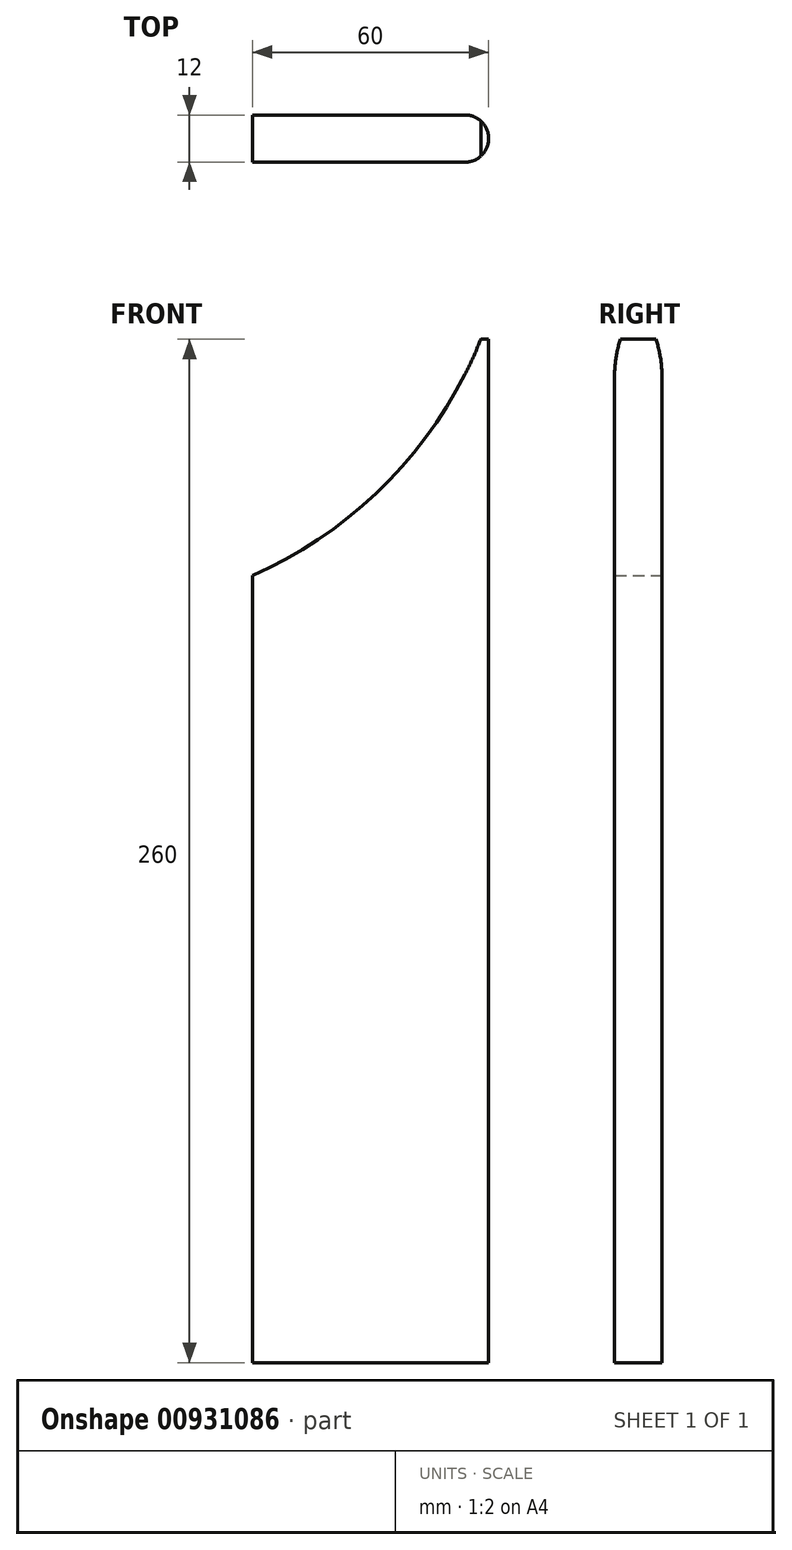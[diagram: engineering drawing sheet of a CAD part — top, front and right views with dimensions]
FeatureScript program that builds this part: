
annotation { "Feature Type Name" : "Feature", "Feature Type Description" : "" }
export const myFeature = defineFeature(function(context is Context, id is Id, definition is map)
    precondition{}
    {
        {
            var Q0;
            Q0=qCreatedBy(makeId("Front.planeOp"),FACE);
            var sketch = newSketch(context, id + "F0", { "sketchPlane" : qUnion([Q0])});
            skLineSegment(sketch, "E0.bottom", {"start": v(0, 0) * mm, "end": v(60, 0) * mm});
            skLineSegment(sketch, "E0.top", {"start": v(58, 260) * mm, "end": v(60, 260) * mm});
            skLineSegment(sketch, "E0.left", {"start": v(0, 0) * mm, "end": v(0, 200) * mm});
            skLineSegment(sketch, "E0.right", {"start": v(60, 0) * mm, "end": v(60, 260) * mm});
            skArc(sketch, "E1", {"start": v(0, 200) * mm, "mid": v(34.91, 224.29) * mm, "end": v(58, 260) * mm});
            skSolve(sketch);
        }
        {
            var Q0;
            Q0=makeQuery(id+"F0.imprint","IMPRINT",FACE,{"disambiguationData":[TD([[makeQuery(id+"F0.imprint","IMPRINT",EDGE,{"derivedFrom":sQuery(id+"F0.wireOp",EDGE,"E0.bottom")}),1.0]])]});
            extrude(context, id + "F1", {"entities" : qUnion([Q0]), "depth" : 12 * mm, "offsetDistance" : 25 * mm});
        }
        {
            var Q0;
            Q0=makeQuery(id+"F1.opExtrude","CAP_EDGE",EDGE,{"disambiguationData":[OSD([sQuery(id+"F0.wireOp",EDGE,"E0.right")])],"isStart":false});
            var Q1;
            Q1=makeQuery(id+"F1.opExtrude","CAP_EDGE",EDGE,{"disambiguationData":[OSD([sQuery(id+"F0.wireOp",EDGE,"E0.right")])],"isStart":true});
            fillet(context, id + "F2", {"entities" : qUnion([Q0, Q1]), "tangentPropagation" : true, "radius" : 6 * mm, "defaultsChanged" : true, "vertexSettings" : [], "allowEdgeOverflow" : false});
        }
    });
